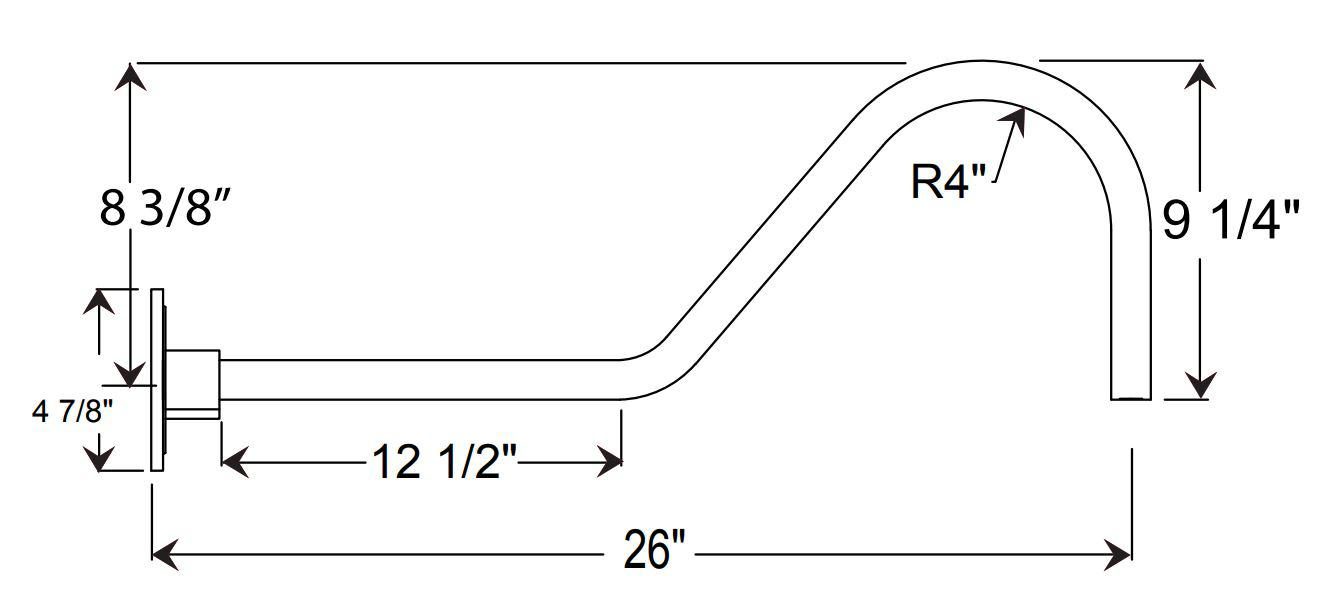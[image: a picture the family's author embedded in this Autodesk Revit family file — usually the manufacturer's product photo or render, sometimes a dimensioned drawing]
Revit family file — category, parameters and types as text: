
# Revit family: Radial 8,12,16,18,20,24 LED
name_source: partatom
category: Lighting Fixtures
units: mm (PartAtom-declared; Revit-internal decimal feet)

## family parameters
Always vertical = Yes
Cut with Voids When Loaded = No
Light Source = Yes
OmniClass Number = 23.80.70.00
OmniClass Title = Lighting
Part Type = Normal
Room Calculation Point = No
Round Connector Dimension = Use Diameter
Shared = No
Work Plane-Based = No

## types (6) — shared parameters
Body Colour = Spun aluminium
Body Material = body
Bulb = Glass
CRI = >90
Canopy Body = body
Color Filter = 16777215
Construction Material = Heavy Duty spun aluminum.
Default Elevation = 0' - 0"
Description = 120-277 Voltage
Dimming = 1%
Dimming Lamp Color Temperature Shift = <None>
Efficiency = 65-125 lumens per watt
INSIDE BODY = Default
Lamp = LED
Life = L70 50,000 hours
Load Classification = Lighting
Manufacturer = ANP Lighting
Photometric Web File = R920-200GLCL-200INC-T15298.IES
Power Factor = 1
Tilt Angle = 90.00°
URL = https://www.anplighting.com
Voltage = 277 V
Warranty = 5 year limited warranty
b = 0' - 2"

## per-type parameters (varying)
| type | Apparent Load | Fixture Diameter | Fixture Height | R908 | R912 | R916 | R918 | R920 | R924 | Wattage Comments | Weight | a |
| R908 | 10 VA | 0' - 8" | 0' - 4 1/2" | Yes | No | No | No | No | No | 10 W | 1.0 lbs | 0' - 8 1/2" |
| R912 | 16 VA | 1' - 0" | 0' - 5 1/4" | No | Yes | No | No | No | No | 16 W | 1.0 lbs | 0' - 9" |
| R916 | 16 VA | 1' - 4" | 0' - 6 3/4" | No | No | Yes | No | No | No | 16 W | 2.0 lbs | 0' - 11" |
| R918 | 24 VA | 1' - 6" | 0' - 7" | No | No | No | Yes | No | No | 24 W | 2.0 lbs | 0' - 11" |
| R920 | 24 VA | 1' - 8" | 0' - 7" | No | No | No | No | Yes | No | 24 W | 2.5 lbs | 0' - 11" |
| R924 | 24 VA | 2' - 0" | 0' - 7" | No | No | No | No | No | Yes | 24 W | 3.0 lbs | 0' - 11" |

note: column(s) folded — value = type name in every type: Model

## geometry (parser evidence)
native form markers: Sweep x39
no freeform markers — native parametric forms only
